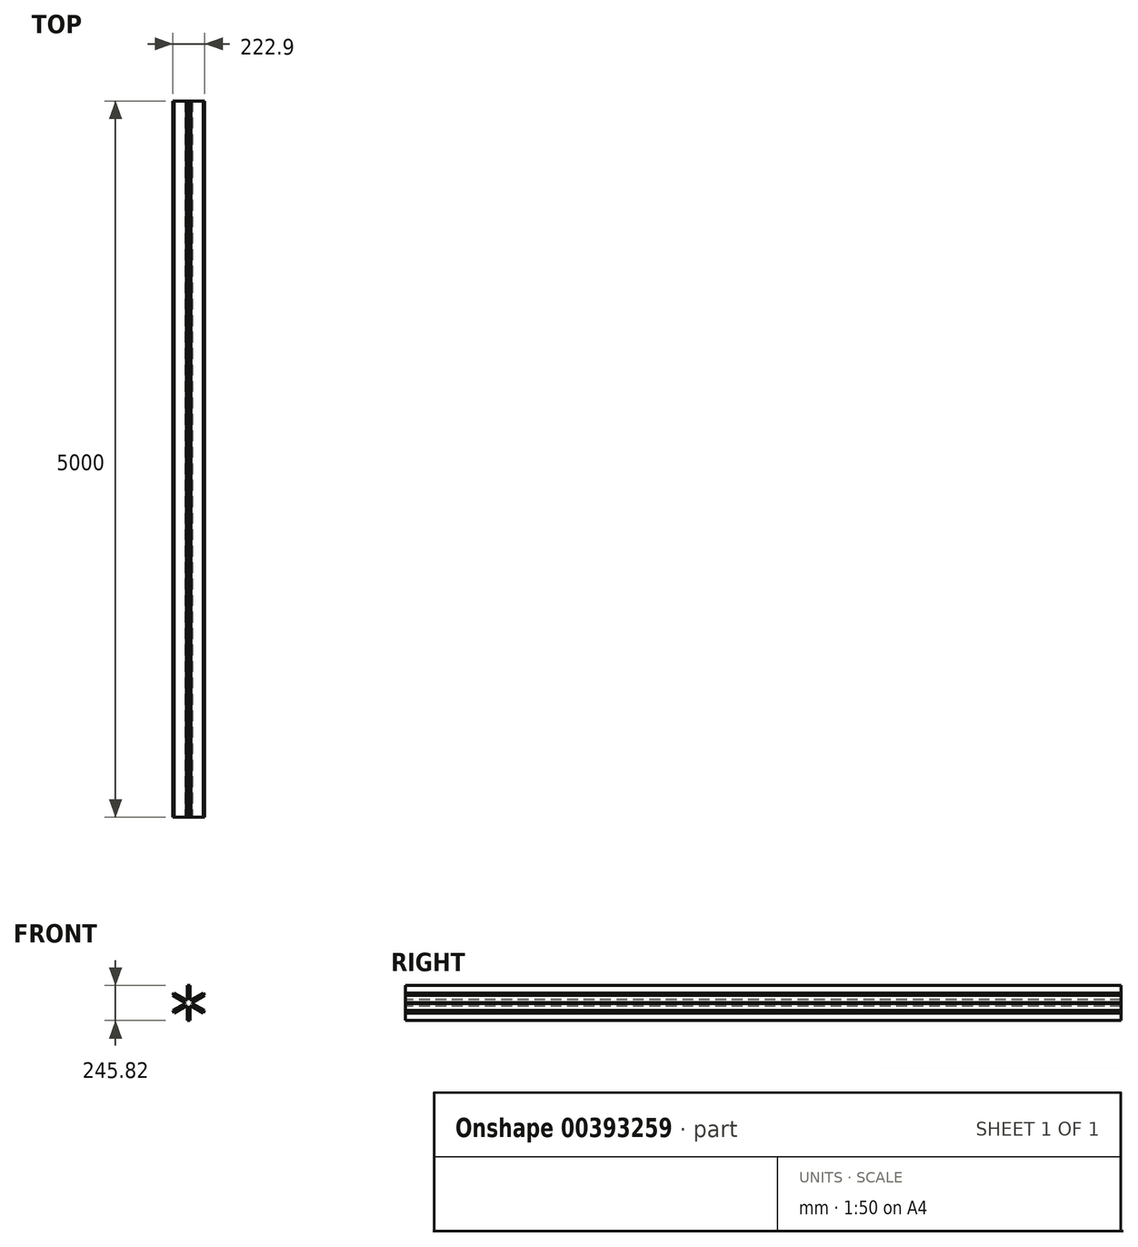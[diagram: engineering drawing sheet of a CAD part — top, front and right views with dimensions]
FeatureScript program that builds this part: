
annotation { "Feature Type Name" : "Feature", "Feature Type Description" : "" }
export const myFeature = defineFeature(function(context is Context, id is Id, definition is map)
    precondition{}
    {
        {
            var Q0;
            Q0=qCreatedBy(makeId("Front.planeOp"),FACE);
            var sketch = newSketch(context, id + "F0", { "sketchPlane" : qUnion([Q0])});
            skCircle(sketch, "E0", {"center": v(0, 0) * mm, "radius": 25 * mm});
            skLineSegment(sketch, "E1", {"start": v(0, 122.91) * mm, "end": v(10, 122.91) * mm});
            skLineSegment(sketch, "E2", {"start": v(10, 122.91) * mm, "end": v(10, 22.91) * mm});
            skLineSegment(sketch, "E3", {"start": v(0, 122.91) * mm, "end": v(-10, 122.91) * mm});
            skLineSegment(sketch, "E4", {"start": v(-10, 122.91) * mm, "end": v(-10, 22.91) * mm});
            skLineSegment(sketch, "E5.1.0", {"start": v(-106.45, 61.46) * mm, "end": v(-101.45, 70.12) * mm});
            skLineSegment(sketch, "E5.1.1", {"start": v(-101.45, 70.12) * mm, "end": v(-14.84, 20.12) * mm});
            skLineSegment(sketch, "E5.1.2", {"start": v(-111.45, 52.8) * mm, "end": v(-24.84, 2.8) * mm});
            skLineSegment(sketch, "E5.1.3", {"start": v(-106.45, 61.46) * mm, "end": v(-111.45, 52.8) * mm});
            skLineSegment(sketch, "E5.2.0", {"start": v(-106.45, -61.46) * mm, "end": v(-111.45, -52.8) * mm});
            skLineSegment(sketch, "E5.2.1", {"start": v(-111.45, -52.8) * mm, "end": v(-24.84, -2.8) * mm});
            skLineSegment(sketch, "E5.2.2", {"start": v(-101.45, -70.12) * mm, "end": v(-14.84, -20.12) * mm});
            skLineSegment(sketch, "E5.2.3", {"start": v(-106.45, -61.46) * mm, "end": v(-101.45, -70.12) * mm});
            skLineSegment(sketch, "E6.3.3.0", {"start": v(-10, -122.91) * mm, "end": v(-10, -22.91) * mm});
            skLineSegment(sketch, "E6.6.3.0", {"start": v(10, -122.91) * mm, "end": v(10, -22.91) * mm});
            skLineSegment(sketch, "E6.8.3.0", {"start": v(0, -122.91) * mm, "end": v(-10, -122.91) * mm});
            skLineSegment(sketch, "E6.9.3.0", {"start": v(0, -122.91) * mm, "end": v(10, -122.91) * mm});
            skLineSegment(sketch, "E6.3.4.0", {"start": v(101.45, -70.12) * mm, "end": v(14.84, -20.12) * mm});
            skLineSegment(sketch, "E6.6.4.0", {"start": v(111.45, -52.8) * mm, "end": v(24.84, -2.8) * mm});
            skLineSegment(sketch, "E6.8.4.0", {"start": v(106.45, -61.46) * mm, "end": v(101.45, -70.12) * mm});
            skLineSegment(sketch, "E6.9.4.0", {"start": v(106.45, -61.46) * mm, "end": v(111.45, -52.8) * mm});
            skLineSegment(sketch, "E6.3.5.0", {"start": v(111.45, 52.8) * mm, "end": v(24.84, 2.8) * mm});
            skLineSegment(sketch, "E6.6.5.0", {"start": v(101.45, 70.12) * mm, "end": v(14.84, 20.12) * mm});
            skLineSegment(sketch, "E6.8.5.0", {"start": v(106.45, 61.46) * mm, "end": v(111.45, 52.8) * mm});
            skLineSegment(sketch, "E6.9.5.0", {"start": v(106.45, 61.46) * mm, "end": v(101.45, 70.12) * mm});
            skSolve(sketch);
        }
        {
            var Q0;
            {var subQ1=sQuery(id+"F0.wireOp",EDGE,"E6.3.5.0");Q0=makeQuery(id+"F0.imprint","IMPRINT",FACE,{"disambiguationData":[TD([[makeQuery(id+"F0.imprint","IMPRINT",EDGE,{"derivedFrom":subQ1}),-1.0]])]});}
            var Q1;
            {var subQ1=sQuery(id+"F0.wireOp",EDGE,"E6.3.4.0");Q1=makeQuery(id+"F0.imprint","IMPRINT",FACE,{"disambiguationData":[TD([[makeQuery(id+"F0.imprint","IMPRINT",EDGE,{"derivedFrom":subQ1}),-1.0]])]});}
            var Q2;
            {var subQ1=sQuery(id+"F0.wireOp",EDGE,"E6.3.3.0");Q2=makeQuery(id+"F0.imprint","IMPRINT",FACE,{"disambiguationData":[TD([[makeQuery(id+"F0.imprint","IMPRINT",EDGE,{"derivedFrom":subQ1}),-1.0]])]});}
            var Q3;
            {var subQ0=sQuery(id+"F0.wireOp",EDGE,"E0");var subQ8=makeQuery(id+"F0.imprint","INTERSECT",VERTEX,{"derivedFrom":[subQ0,sQuery(id+"F0.wireOp",EDGE,"E6.3.5.0")]});Q3=makeQuery(id+"F0.imprint","IMPRINT",FACE,{"disambiguationData":[TD([[makeQuery(id+"F0.imprint","IMPRINT",EDGE,{"disambiguationData":[TD([[subQ8,-1.0]])],"derivedFrom":subQ0}),1.0]])]});}
            var Q4;
            Q4=makeQuery(id+"F0.imprint","IMPRINT",FACE,{"disambiguationData":[TD([[makeQuery(id+"F0.imprint","IMPRINT",EDGE,{"derivedFrom":sQuery(id+"F0.wireOp",EDGE,"E5.2.0")}),-1.0]])]});
            var Q5;
            Q5=makeQuery(id+"F0.imprint","IMPRINT",FACE,{"disambiguationData":[TD([[makeQuery(id+"F0.imprint","IMPRINT",EDGE,{"derivedFrom":sQuery(id+"F0.wireOp",EDGE,"E5.1.0")}),-1.0]])]});
            var Q6;
            Q6=makeQuery(id+"F0.imprint","IMPRINT",FACE,{"disambiguationData":[TD([[makeQuery(id+"F0.imprint","IMPRINT",EDGE,{"derivedFrom":sQuery(id+"F0.wireOp",EDGE,"E1")}),-1.0]])]});
            extrude(context, id + "F1", {"entities" : qUnion([Q0, Q1, Q2, Q3, Q4, Q5, Q6]), "oppositeDirection" : true, "depth" : 5000 * mm});
        }
    });
